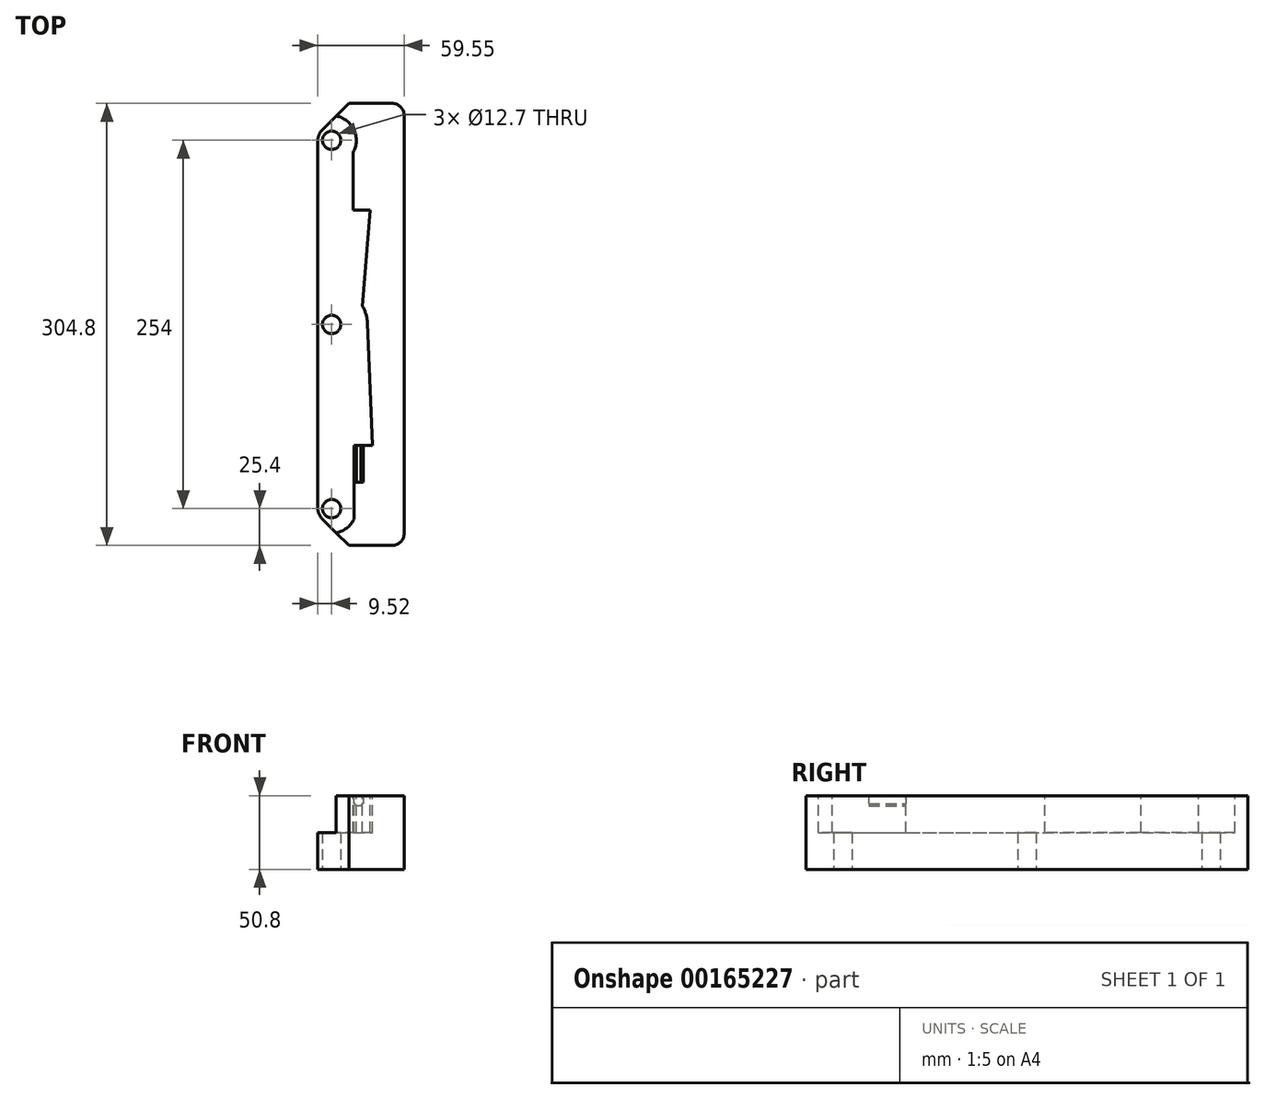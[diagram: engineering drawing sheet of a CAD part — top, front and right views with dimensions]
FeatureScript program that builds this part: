
annotation { "Feature Type Name" : "Feature", "Feature Type Description" : "" }
export const myFeature = defineFeature(function(context is Context, id is Id, definition is map)
    precondition{}
    {
        {
            var Q0;
            Q0=qCreatedBy(makeId("Top.planeOp"),FACE);
            var sketch = newSketch(context, id + "F0", { "sketchPlane" : qUnion([Q0])});
            skCircle(sketch, "E0", {"center": v(-11.93, -127) * mm, "radius": 6.35 * mm});
            skArc(sketch, "E1", {"start": v(-21.45, -127) * mm, "mid": v(-20.73, -130.65) * mm, "end": v(-18.66, -133.74) * mm});
            skLineSegment(sketch, "E2", {"start": v(-21.45, -127) * mm, "end": v(-21.45, 127) * mm});
            skArc(sketch, "E3", {"start": v(-18.66, 133.74) * mm, "mid": v(-20.73, 130.65) * mm, "end": v(-21.45, 127) * mm});
            skCircle(sketch, "E4", {"center": v(-11.93, 127) * mm, "radius": 6.35 * mm});
            skLineSegment(sketch, "E5", {"start": v(-18.66, -133.74) * mm, "end": v(0, -152.4) * mm});
            skLineSegment(sketch, "E6", {"start": v(0, -152.4) * mm, "end": v(38.1, -152.4) * mm});
            skLineSegment(sketch, "E7", {"start": v(38.1, -152.4) * mm, "end": v(38.1, 152.4) * mm});
            skLineSegment(sketch, "E8", {"start": v(38.1, 152.4) * mm, "end": v(0, 152.4) * mm});
            skLineSegment(sketch, "E9", {"start": v(0, 152.4) * mm, "end": v(-18.66, 133.74) * mm});
            skLineSegment(sketch, "E10", {"start": v(0, -152.4) * mm, "end": v(0, 152.4) * mm, "construction": true});
            skLineSegment(sketch, "E11", {"start": v(-11.93, 127) * mm, "end": v(-11.93, -127) * mm, "construction": true});
            skCircle(sketch, "E12", {"center": v(-11.93, 0) * mm, "radius": 6.35 * mm});
            skLineSegment(sketch, "E13", {"start": v(-11.93, 0) * mm, "end": v(0, 0) * mm, "construction": true});
            skSolve(sketch);
        }
        {
            var Q0;
            Q0=qSketchRegion(id+"F0",true);
            extrude(context, id + "F1", {"entities" : qUnion([Q0]), "depth" : 50.8 * mm});
        }
        {
            var Q0;
            Q0=makeQuery(id+"F1.opExtrude","SWEPT_EDGE",EDGE,{"disambiguationData":[OSD([sQuery(id+"F0.wireOp",EDGE,"E7"),sQuery(id+"F0.wireOp",EDGE,"E8")])]});
            var Q1;
            Q1=makeQuery(id+"F1.opExtrude","SWEPT_EDGE",EDGE,{"disambiguationData":[OSD([sQuery(id+"F0.wireOp",EDGE,"E6"),sQuery(id+"F0.wireOp",EDGE,"E7")])]});
            var Q2;
            Q2=makeQuery(id+"FgZ2pZbpDbev36X_1.opExtrude","SWEPT_EDGE",EDGE,{"disambiguationData":[OSD([sQuery(id+"F8tsPCVh05mAfvm_1.wireOp",EDGE,"uFLmPw9w-U9YU-98V4-AHxu-UnPQV13gNSsj.top"),sQuery(id+"F8tsPCVh05mAfvm_1.wireOp",EDGE,"uFLmPw9w-U9YU-98V4-AHxu-UnPQV13gNSsj.right")])]});
            var Q3;
            Q3=makeQuery(id+"FgZ2pZbpDbev36X_1.opExtrude","SWEPT_EDGE",EDGE,{"disambiguationData":[OSD([sQuery(id+"F8tsPCVh05mAfvm_1.wireOp",EDGE,"nV6HWze4-40uo-DJtJ-M636-7v8EuhWib6oK.top"),sQuery(id+"F8tsPCVh05mAfvm_1.wireOp",EDGE,"nV6HWze4-40uo-DJtJ-M636-7v8EuhWib6oK.right")])]});
            fillet(context, id + "F2", {"entities" : qUnion([Q0, Q1, Q2, Q3]), "radius" : 8.33 * mm, "tangentPropagation" : true, "allowEdgeOverflow" : false});
        }
        {
            var Q0;
            Q0=makeQuery(id+"F1.opExtrude","CAP_FACE",FACE,{"disambiguationData":[OSD([sQuery(id+"F0.wireOp",EDGE,"E0"),sQuery(id+"F0.wireOp",EDGE,"E1"),sQuery(id+"F0.wireOp",EDGE,"E2"),sQuery(id+"F0.wireOp",EDGE,"E3"),sQuery(id+"F0.wireOp",EDGE,"E4"),sQuery(id+"F0.wireOp",EDGE,"E5"),sQuery(id+"F0.wireOp",EDGE,"E6"),sQuery(id+"F0.wireOp",EDGE,"E7"),sQuery(id+"F0.wireOp",EDGE,"E8"),sQuery(id+"F0.wireOp",EDGE,"E9"),sQuery(id+"F0.wireOp",EDGE,"E12")])],"isStart":false});
            var sketch = newSketch(context, id + "F3", { "sketchPlane" : qUnion([Q0])});
            skArc(sketch, "E14", {"start": v(-8.74, -143.66) * mm, "mid": v(-1.57, -140.43) * mm, "end": v(3.38, -134.3) * mm});
            skLineSegment(sketch, "E15", {"start": v(-8.74, -143.66) * mm, "end": v(-18.66, -133.74) * mm});
            skLineSegment(sketch, "E16", {"start": v(-21.45, -127) * mm, "end": v(-21.45, 127) * mm});
            skArc(sketch, "E17", {"start": v(-21.45, -127) * mm, "mid": v(-20.73, -130.65) * mm, "end": v(-18.66, -133.74) * mm});
            skLineSegment(sketch, "E18", {"start": v(3.38, -134.3) * mm, "end": v(3.38, -83.5) * mm});
            skLineSegment(sketch, "E19", {"start": v(-11.93, -127) * mm, "end": v(3.38, -127) * mm, "construction": true});
            skLineSegment(sketch, "E20", {"start": v(16.08, -83.5) * mm, "end": v(12.75, 0.97) * mm});
            skArc(sketch, "E21", {"start": v(12.75, 0.97) * mm, "mid": v(11.77, 6.96) * mm, "end": v(9.36, 12.52) * mm});
            skLineSegment(sketch, "E22", {"start": v(3.38, -83.5) * mm, "end": v(16.08, -83.5) * mm});
            skArc(sketch, "E23", {"start": v(-18.66, 133.74) * mm, "mid": v(-20.73, 130.65) * mm, "end": v(-21.45, 127) * mm});
            skArc(sketch, "E24", {"start": v(2.84, 118.67) * mm, "mid": v(3.46, 134.13) * mm, "end": v(-8.74, 143.66) * mm});
            skLineSegment(sketch, "E25", {"start": v(-8.74, 143.66) * mm, "end": v(-18.66, 133.74) * mm});
            skLineSegment(sketch, "E26", {"start": v(2.84, 118.67) * mm, "end": v(2.84, 78.73) * mm});
            skLineSegment(sketch, "E27", {"start": v(2.84, 78.73) * mm, "end": v(14.46, 78.73) * mm});
            skLineSegment(sketch, "E28", {"start": v(14.46, 78.73) * mm, "end": v(9.36, 12.52) * mm});
            skSolve(sketch);
        }
        {
            var Q0;
            Q0 = qSketchRegion(id + "F3", true);
            extrude(context, id + "F4", {"entities" : qUnion([Q0]), "operationType" : NewBodyOperationType.REMOVE, "oppositeDirection" : true, "depth" : 25.4 * mm});
        }
        {
            var Q0;
            Q0=makeQuery(id+"F4.boolean.opBoolean","COPY",FACE,{"derivedFrom":makeQuery(id+"F4.opExtrude","SWEPT_FACE",FACE,{"disambiguationData":[OSD([sQuery(id+"F3.wireOp",EDGE,"E22")])]})});
            var sketch = newSketch(context, id + "F5", { "sketchPlane" : qUnion([Q0])});
            skLineSegment(sketch, "E29", {"start": v(-9.73, 50.8) * mm, "end": v(-9.73, 45.24) * mm});
            skLineSegment(sketch, "E30", {"start": v(-9.73, 45.24) * mm, "end": v(-8.94, 45.24) * mm});
            skLineSegment(sketch, "E31", {"start": v(-8.94, 45.24) * mm, "end": v(-8.94, 44.45) * mm});
            skLineSegment(sketch, "E32", {"start": v(-8.94, 44.45) * mm, "end": v(-8.14, 44.45) * mm});
            skLineSegment(sketch, "E33", {"start": v(-8.14, 44.45) * mm, "end": v(-8.14, 43.66) * mm});
            skLineSegment(sketch, "E34", {"start": v(-8.14, 43.66) * mm, "end": v(-4.97, 43.66) * mm});
            skLineSegment(sketch, "E35", {"start": v(-4.97, 43.66) * mm, "end": v(-4.97, 44.45) * mm});
            skLineSegment(sketch, "E36", {"start": v(-4.97, 44.45) * mm, "end": v(-4.17, 44.45) * mm});
            skLineSegment(sketch, "E37", {"start": v(-4.17, 44.45) * mm, "end": v(-4.17, 45.24) * mm});
            skLineSegment(sketch, "E38", {"start": v(-4.17, 45.24) * mm, "end": v(-3.38, 45.24) * mm});
            skLineSegment(sketch, "E39", {"start": v(-3.38, 45.24) * mm, "end": v(-3.38, 50.8) * mm});
            skLineSegment(sketch, "E40", {"start": v(-3.38, 50.8) * mm, "end": v(-9.73, 50.8) * mm});
            skLineSegment(sketch, "E41", {"start": v(-8.94, 45.24) * mm, "end": v(-4.17, 45.24) * mm, "construction": true});
            skSolve(sketch);
        }
        {
            var Q0;
            Q0=makeQuery(id+"F5.imprint","IMPRINT",FACE,{"disambiguationData":[TD([[makeQuery(id+"F5.imprint","IMPRINT",EDGE,{"derivedFrom":sQuery(id+"F5.wireOp",EDGE,"E29")}),1.0]])]});
            extrude(context, id + "F6", {"entities" : qUnion([Q0]), "operationType" : NewBodyOperationType.REMOVE, "oppositeDirection" : true, "depth" : 25.4 * mm});
        }
    });
